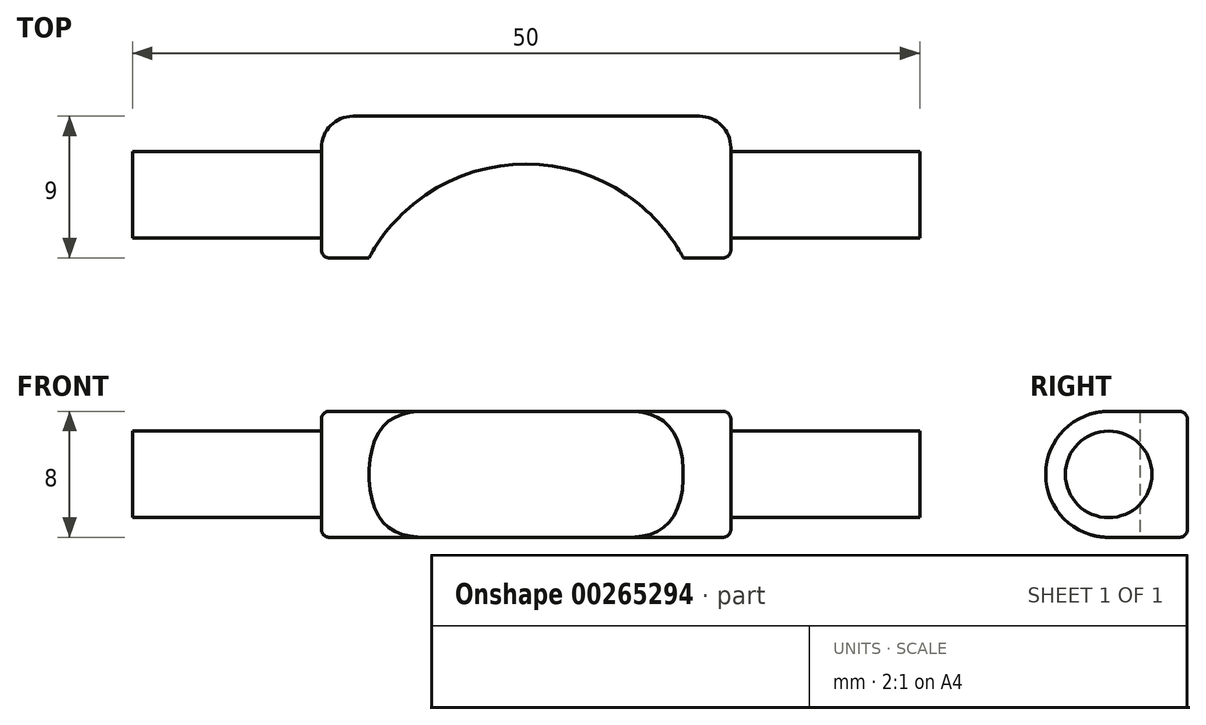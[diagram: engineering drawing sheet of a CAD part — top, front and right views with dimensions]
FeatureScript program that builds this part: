
annotation { "Feature Type Name" : "Feature", "Feature Type Description" : "" }
export const myFeature = defineFeature(function(context is Context, id is Id, definition is map)
    precondition{}
    {
        {
            var Q0;
            Q0=qCreatedBy(makeId("Right.planeOp"),FACE);
            var sketch = newSketch(context, id + "F0", { "sketchPlane" : qUnion([Q0])});
            skCircle(sketch, "E0", {"center": v(0, 0) * mm, "radius": 2.75 * mm});
            skCircle(sketch, "E1", {"center": v(0, 0) * mm, "radius": 4 * mm});
            skLineSegment(sketch, "E2.bottom", {"start": v(0, -4) * mm, "end": v(5, -4) * mm});
            skLineSegment(sketch, "E2.top", {"start": v(0, 4) * mm, "end": v(5, 4) * mm});
            skLineSegment(sketch, "E2.right", {"start": v(5, -4) * mm, "end": v(5, 4) * mm});
            skSolve(sketch);
        }
        {
            var Q0;
            Q0=makeQuery(id+"F0.imprint","IMPRINT",FACE,{"disambiguationData":[TD([[makeQuery(id+"F0.imprint","IMPRINT",EDGE,{"derivedFrom":sQuery(id+"F0.wireOp",EDGE,"E0")}),1.0]])]});
            extrude(context, id + "F1", {"entities" : qUnion([Q0]), "depth" : 25 * mm});
        }
        {
            var Q0;
            Q0 = qSketchRegion(id + "F0", true);
            extrude(context, id + "F2", {"entities" : qUnion([Q0]), "operationType" : NewBodyOperationType.ADD, "depth" : 13 * mm});
        }
        {
            var Q0;
            Q0=makeQuery(id+"F2.opExtrude","CAP_EDGE",EDGE,{"disambiguationData":[OSD([sQuery(id+"F0.wireOp",EDGE,"E2.right")])],"isStart":false});
            fillet(context, id + "F3", {"entities" : qUnion([Q0]), "radius" : 2 * mm, "tangentPropagation" : true, "allowEdgeOverflow" : false});
        }
        {
            var Q0;
            Q0=qCreatedBy(makeId("Top.planeOp"),FACE);
            var sketch = newSketch(context, id + "F4", { "sketchPlane" : qUnion([Q0])});
            skLineSegment(sketch, "E3.bottom", {"start": v(0, -4.03) * mm, "end": v(10, -4.03) * mm});
            skLineSegment(sketch, "E3.top", {"start": v(0, 1.97) * mm, "end": v(10, 1.97) * mm, "construction": true});
            skLineSegment(sketch, "E3.left", {"start": v(0, -4.03) * mm, "end": v(0, 1.97) * mm});
            skLineSegment(sketch, "E3.right", {"start": v(10, -4.03) * mm, "end": v(10, 1.97) * mm, "construction": true});
            skArc(sketch, "E4", {"start": v(10, -4.03) * mm, "mid": v(5.83, 0.35) * mm, "end": v(0, 1.97) * mm});
            skSolve(sketch);
        }
        {
            var Q0;
            Q0 = qSketchRegion(id + "F4", true);
            extrude(context, id + "F5", {"entities" : qUnion([Q0]), "operationType" : NewBodyOperationType.REMOVE, "depth" : 25 * mm, "hasSecondDirection" : true, "secondDirectionOppositeDirection" : true, "secondDirectionDepth" : 25 * mm});
        }
        {
            var Q0;
            Q0=makeQuery(id+"F1.opExtrude","SWEPT_BODY",BODY,{"disambiguationData":[OSD([sQuery(id+"F0.wireOp",EDGE,"E0")])]});
            var Q1;
            {var subQ0=sQuery(id+"F0.wireOp",EDGE,"E0");Q1=makeQuery(id+"F2.boolean.opBoolean","MERGE",FACE,{"derivedFrom":[makeQuery(id+"F1.opExtrude","CAP_FACE",FACE,{"disambiguationData":[OSD([subQ0])],"isStart":true}),makeQuery(id+"F2.opExtrude","CAP_FACE",FACE,{"disambiguationData":[OSD([subQ0,sQuery(id+"F0.wireOp",EDGE,"E1")])],"isStart":true})]});}
            mirror(context, id + "F6", {"operationType" : NewBodyOperationType.ADD, "entities" : qUnion([Q0]), "mirrorPlane" : qUnion([Q1])});
        }
        {
            var Q0;
            Q0=makeQuery(id+"F2.opExtrude","CAP_EDGE",EDGE,{"disambiguationData":[OSD([sQuery(id+"F0.wireOp",EDGE,"E1")])],"isStart":false});
            var Q1;
            Q1=makeQuery(id+"F6.opPattern","COPY",EDGE,{"derivedFrom":makeQuery(id+"F2.opExtrude","CAP_EDGE",EDGE,{"disambiguationData":[OSD([sQuery(id+"F0.wireOp",EDGE,"E1")])],"isStart":false}),"instanceName":"1"});
            var Q2;
            {var subQ0=makeQuery(id+"F5.boolean.opBoolean","INTERSECT",EDGE,{"derivedFrom":[makeQuery(id+"F2.opExtrude","SWEPT_FACE",FACE,{"disambiguationData":[OSD([sQuery(id+"F0.wireOp",EDGE,"E1")])]}),makeQuery(id+"F5.opExtrude","SWEPT_FACE",FACE,{"disambiguationData":[OSD([sQuery(id+"F4.wireOp",EDGE,"E4")])]})]});Q2=makeQuery(id+"F6.boolean.opBoolean","MERGE",EDGE,{"derivedFrom":[subQ0,makeQuery(id+"F6.opPattern","COPY",EDGE,{"derivedFrom":subQ0,"instanceName":"1"})]});}
            fillet(context, id + "F7", {"entities" : qUnion([Q0, Q1, Q2]), "radius" : .5 * mm, "tangentPropagation" : true, "allowEdgeOverflow" : false});
        }
    });
